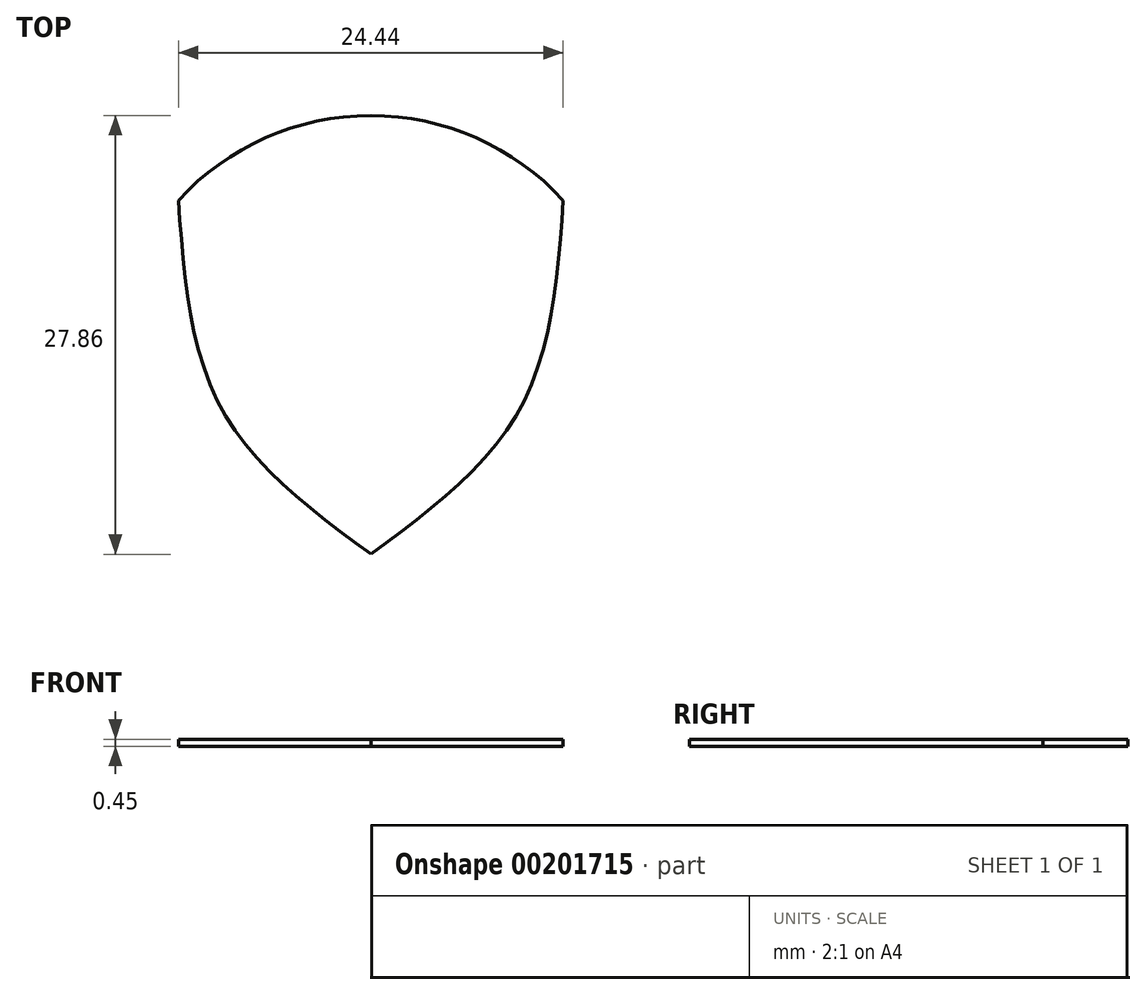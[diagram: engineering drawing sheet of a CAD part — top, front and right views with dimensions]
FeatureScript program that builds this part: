
annotation { "Feature Type Name" : "Feature", "Feature Type Description" : "" }
export const myFeature = defineFeature(function(context is Context, id is Id, definition is map)
    precondition{}
    {
        {
            var Q0;
            Q0=qCreatedBy(makeId("Top.planeOp"),FACE);
            var sketch = newSketch(context, id + "F0", { "sketchPlane" : qUnion([Q0])});
            skArc(sketch, "E0", {"start": v(12.22, 0) * mm, "mid": v(0, 5.39) * mm, "end": v(-12.22, 0) * mm});
            skFitSpline(sketch, "E1", {"points": [v(-12.22, 0) * mm, v(-9.46, -13.27) * mm, v(0, -22.47) * mm], "startDerivative": vector(2.08, -28.33) * mm, "endDerivative": vector(22.41, -16.57) * mm});
            skFitSpline(sketch, "E2.MirrorCS", {"points": [v(12.22, 0) * mm, v(9.46, -13.27) * mm, v(0, -22.47) * mm], "startDerivative": vector(-2.08, -28.33) * mm, "endDerivative": vector(-22.41, -16.57) * mm});
            skSolve(sketch);
        }
        {
            var Q0;
            Q0=makeQuery(id+"F0.imprint","IMPRINT",FACE,{"disambiguationData":[TD([[makeQuery(id+"F0.imprint","IMPRINT",EDGE,{"derivedFrom":sQuery(id+"F0.wireOp",EDGE,"E0")}),1.0]])]});
            extrude(context, id + "F1", {"entities" : qUnion([Q0]), "depth" : 0.45 * mm});
        }
    });
